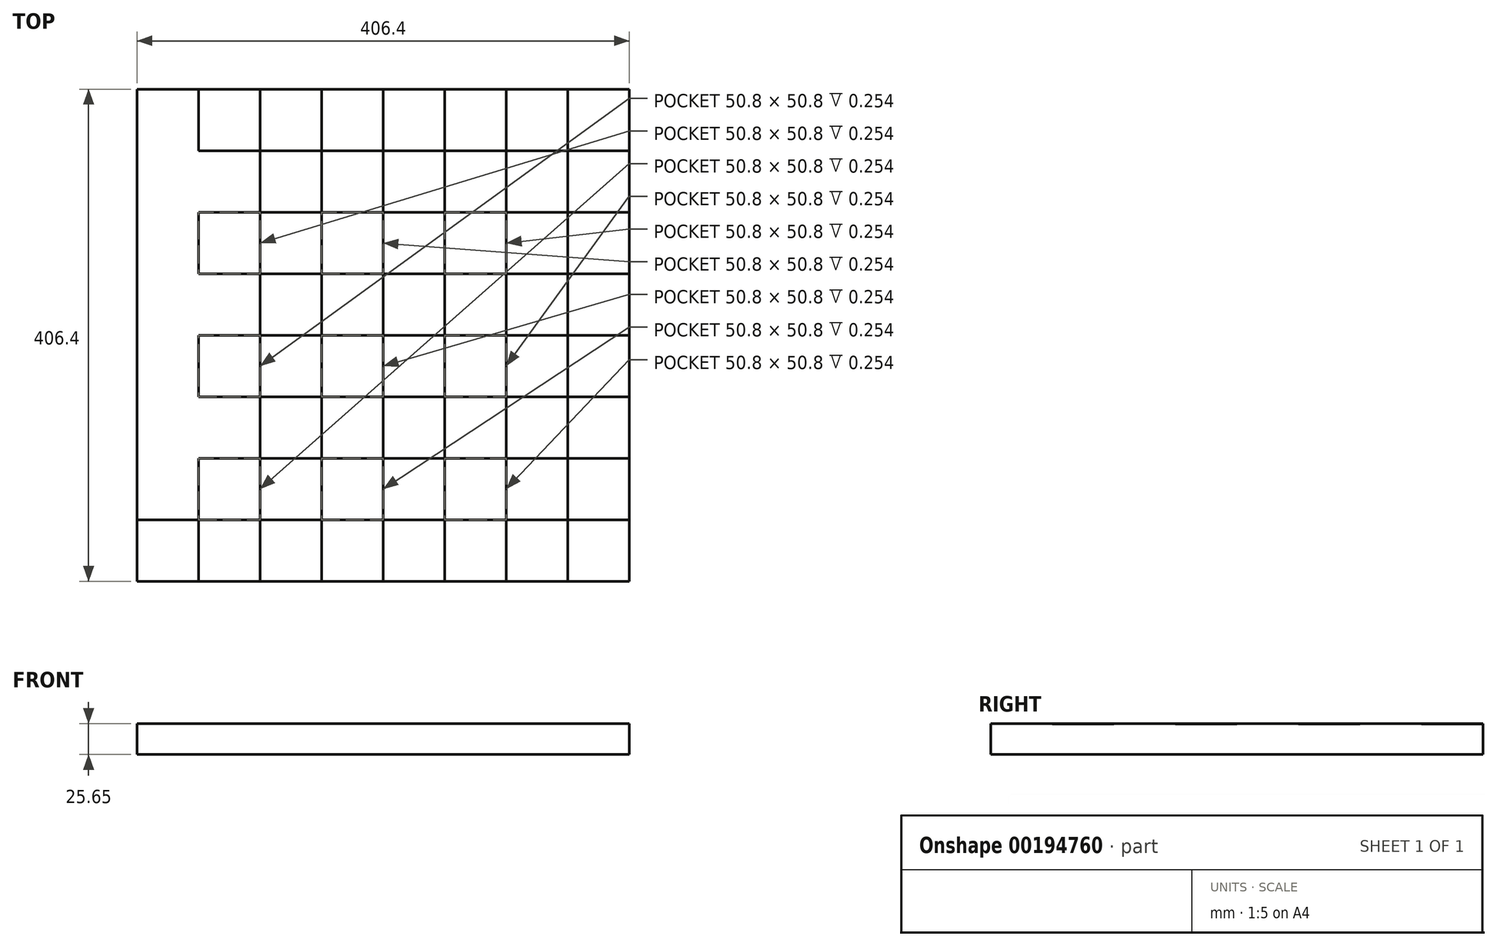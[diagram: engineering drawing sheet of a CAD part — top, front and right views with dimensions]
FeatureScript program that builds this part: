
annotation { "Feature Type Name" : "Feature", "Feature Type Description" : "" }
export const myFeature = defineFeature(function(context is Context, id is Id, definition is map)
    precondition{}
    {
        {
            var Q0;
            Q0=qCreatedBy(makeId("Top.planeOp"),FACE);
            var sketch = newSketch(context, id + "F0", { "sketchPlane" : qUnion([Q0])});
            skLineSegment(sketch, "E0.bottom", {"start": v(-124.17, 310.54) * mm, "end": v(282.23, 310.54) * mm});
            skLineSegment(sketch, "E0.top", {"start": v(-124.17, -95.86) * mm, "end": v(282.23, -95.86) * mm});
            skLineSegment(sketch, "E0.left", {"start": v(-124.17, 310.54) * mm, "end": v(-124.17, -95.86) * mm});
            skLineSegment(sketch, "E0.right", {"start": v(282.23, 310.54) * mm, "end": v(282.23, -95.86) * mm});
            skSolve(sketch);
        }
        {
            var Q0;
            Q0=makeQuery(id+"F0.imprint","IMPRINT",FACE,{"disambiguationData":[TD([[makeQuery(id+"F0.imprint","IMPRINT",EDGE,{"derivedFrom":sQuery(id+"F0.wireOp",EDGE,"E0.bottom")}),-1.0]])]});
            extrude(context, id + "F1", {"entities" : qUnion([Q0]), "depth" : 25.4 * mm});
        }
        {
            var Q0;
            Q0=makeQuery(id+"F1.opExtrude","CAP_FACE",FACE,{"disambiguationData":[OSD([sQuery(id+"F0.wireOp",EDGE,"E0.bottom"),sQuery(id+"F0.wireOp",EDGE,"E0.top"),sQuery(id+"F0.wireOp",EDGE,"E0.left"),sQuery(id+"F0.wireOp",EDGE,"E0.right")])],"isStart":false});
            var sketch = newSketch(context, id + "F2", { "sketchPlane" : qUnion([Q0])});
            skLineSegment(sketch, "E1.bottom", {"start": v(-124.17, 310.54) * mm, "end": v(-73.37, 310.54) * mm});
            skLineSegment(sketch, "E1.top", {"start": v(-124.17, 259.74) * mm, "end": v(-73.37, 259.74) * mm});
            skLineSegment(sketch, "E1.left", {"start": v(-124.17, 310.54) * mm, "end": v(-124.17, 259.74) * mm});
            skLineSegment(sketch, "E1.right", {"start": v(-73.37, 310.54) * mm, "end": v(-73.37, 259.74) * mm});
            skLineSegment(sketch, "E2.bottom", {"start": v(-73.37, 259.74) * mm, "end": v(-22.57, 259.74) * mm});
            skLineSegment(sketch, "E2.top", {"start": v(-73.37, 310.54) * mm, "end": v(-22.57, 310.54) * mm});
            skLineSegment(sketch, "E2.left", {"start": v(-73.37, 259.74) * mm, "end": v(-73.37, 310.54) * mm});
            skLineSegment(sketch, "E2.right", {"start": v(-22.57, 259.74) * mm, "end": v(-22.57, 310.54) * mm});
            skLineSegment(sketch, "E3.bottom", {"start": v(-22.57, 259.74) * mm, "end": v(28.23, 259.74) * mm});
            skLineSegment(sketch, "E3.top", {"start": v(-22.57, 310.54) * mm, "end": v(28.23, 310.54) * mm});
            skLineSegment(sketch, "E3.right", {"start": v(28.23, 259.74) * mm, "end": v(28.23, 310.54) * mm});
            skLineSegment(sketch, "E4.bottom", {"start": v(28.23, 259.74) * mm, "end": v(28.23, 259.74) * mm});
            skLineSegment(sketch, "E4.top", {"start": v(28.23, 310.54) * mm, "end": v(28.23, 310.54) * mm});
            skLineSegment(sketch, "E5.bottom", {"start": v(28.23, 259.74) * mm, "end": v(79.03, 259.74) * mm});
            skLineSegment(sketch, "E5.top", {"start": v(28.23, 310.54) * mm, "end": v(79.03, 310.54) * mm});
            skLineSegment(sketch, "E5.right", {"start": v(79.03, 259.74) * mm, "end": v(79.03, 310.54) * mm});
            skLineSegment(sketch, "E6.bottom", {"start": v(79.03, 259.74) * mm, "end": v(129.83, 259.74) * mm});
            skLineSegment(sketch, "E6.top", {"start": v(79.03, 310.54) * mm, "end": v(129.83, 310.54) * mm});
            skLineSegment(sketch, "E6.right", {"start": v(129.83, 259.74) * mm, "end": v(129.83, 310.54) * mm});
            skLineSegment(sketch, "E7.bottom", {"start": v(129.83, 259.74) * mm, "end": v(180.63, 259.74) * mm});
            skLineSegment(sketch, "E7.top", {"start": v(129.83, 310.54) * mm, "end": v(180.63, 310.54) * mm});
            skLineSegment(sketch, "E7.right", {"start": v(180.63, 259.74) * mm, "end": v(180.63, 310.54) * mm});
            skLineSegment(sketch, "E8.bottom", {"start": v(180.63, 259.74) * mm, "end": v(231.43, 259.74) * mm});
            skLineSegment(sketch, "E8.top", {"start": v(180.63, 310.54) * mm, "end": v(231.43, 310.54) * mm});
            skLineSegment(sketch, "E8.right", {"start": v(231.43, 259.74) * mm, "end": v(231.43, 310.54) * mm});
            skLineSegment(sketch, "E9.bottom", {"start": v(231.43, 259.74) * mm, "end": v(282.23, 259.74) * mm});
            skLineSegment(sketch, "E9.top", {"start": v(231.43, 310.54) * mm, "end": v(282.23, 310.54) * mm});
            skLineSegment(sketch, "E9.right", {"start": v(282.23, 259.74) * mm, "end": v(282.23, 310.54) * mm});
            skLineSegment(sketch, "E10.bottom", {"start": v(-124.17, -95.86) * mm, "end": v(-73.37, -95.86) * mm});
            skLineSegment(sketch, "E10.top", {"start": v(-124.17, -45.06) * mm, "end": v(-73.37, -45.06) * mm});
            skLineSegment(sketch, "E10.left", {"start": v(-124.17, -95.86) * mm, "end": v(-124.17, -45.06) * mm});
            skLineSegment(sketch, "E10.right", {"start": v(-73.37, -95.86) * mm, "end": v(-73.37, -45.06) * mm});
            skLineSegment(sketch, "E11.bottom", {"start": v(-73.37, -95.86) * mm, "end": v(-22.57, -95.86) * mm});
            skLineSegment(sketch, "E11.top", {"start": v(-73.37, -45.06) * mm, "end": v(-22.57, -45.06) * mm});
            skLineSegment(sketch, "E11.right", {"start": v(-22.57, -95.86) * mm, "end": v(-22.57, -45.06) * mm});
            skLineSegment(sketch, "E12.bottom", {"start": v(-22.57, -95.86) * mm, "end": v(28.23, -95.86) * mm});
            skLineSegment(sketch, "E12.top", {"start": v(-22.57, -45.06) * mm, "end": v(28.23, -45.06) * mm});
            skLineSegment(sketch, "E12.right", {"start": v(28.23, -95.86) * mm, "end": v(28.23, -45.06) * mm});
            skLineSegment(sketch, "E13.bottom", {"start": v(28.23, -95.86) * mm, "end": v(79.03, -95.86) * mm});
            skLineSegment(sketch, "E13.top", {"start": v(28.23, -45.06) * mm, "end": v(79.03, -45.06) * mm});
            skLineSegment(sketch, "E13.right", {"start": v(79.03, -95.86) * mm, "end": v(79.03, -45.06) * mm});
            skLineSegment(sketch, "E14.bottom", {"start": v(79.03, -95.86) * mm, "end": v(129.83, -95.86) * mm});
            skLineSegment(sketch, "E14.top", {"start": v(79.03, -45.06) * mm, "end": v(129.83, -45.06) * mm});
            skLineSegment(sketch, "E14.right", {"start": v(129.83, -95.86) * mm, "end": v(129.83, -45.06) * mm});
            skLineSegment(sketch, "E15.bottom", {"start": v(129.83, -95.86) * mm, "end": v(180.63, -95.86) * mm});
            skLineSegment(sketch, "E15.top", {"start": v(129.83, -45.06) * mm, "end": v(180.63, -45.06) * mm});
            skLineSegment(sketch, "E15.right", {"start": v(180.63, -95.86) * mm, "end": v(180.63, -45.06) * mm});
            skLineSegment(sketch, "E16.bottom", {"start": v(180.63, -95.86) * mm, "end": v(231.43, -95.86) * mm});
            skLineSegment(sketch, "E16.top", {"start": v(180.63, -45.06) * mm, "end": v(231.43, -45.06) * mm});
            skLineSegment(sketch, "E16.right", {"start": v(231.43, -95.86) * mm, "end": v(231.43, -45.06) * mm});
            skLineSegment(sketch, "E17.bottom", {"start": v(231.43, -95.86) * mm, "end": v(282.23, -95.86) * mm});
            skLineSegment(sketch, "E17.top", {"start": v(231.43, -45.06) * mm, "end": v(282.23, -45.06) * mm});
            skLineSegment(sketch, "E17.right", {"start": v(282.23, -95.86) * mm, "end": v(282.23, -45.06) * mm});
            skLineSegment(sketch, "E18.bottom", {"start": v(-73.37, 259.74) * mm, "end": v(-124.17, 259.74) * mm});
            skLineSegment(sketch, "E18.top", {"start": v(-73.37, 208.94) * mm, "end": v(-124.17, 208.94) * mm});
            skLineSegment(sketch, "E18.left", {"start": v(-73.37, 259.74) * mm, "end": v(-73.37, 208.94) * mm});
            skLineSegment(sketch, "E18.right", {"start": v(-124.17, 259.74) * mm, "end": v(-124.17, 208.94) * mm});
            skLineSegment(sketch, "E19.top", {"start": v(-73.37, 158.14) * mm, "end": v(-124.17, 158.14) * mm});
            skLineSegment(sketch, "E19.left", {"start": v(-73.37, 208.94) * mm, "end": v(-73.37, 158.14) * mm});
            skLineSegment(sketch, "E19.right", {"start": v(-124.17, 208.94) * mm, "end": v(-124.17, 158.14) * mm});
            skLineSegment(sketch, "E20.bottom", {"start": v(-124.17, 158.14) * mm, "end": v(-73.37, 158.14) * mm});
            skLineSegment(sketch, "E20.top", {"start": v(-124.17, 107.34) * mm, "end": v(-73.37, 107.34) * mm});
            skLineSegment(sketch, "E20.left", {"start": v(-124.17, 158.14) * mm, "end": v(-124.17, 107.34) * mm});
            skLineSegment(sketch, "E20.right", {"start": v(-73.37, 158.14) * mm, "end": v(-73.37, 107.34) * mm});
            skLineSegment(sketch, "E21.top", {"start": v(-124.17, 56.54) * mm, "end": v(-73.37, 56.54) * mm});
            skLineSegment(sketch, "E21.left", {"start": v(-124.17, 107.34) * mm, "end": v(-124.17, 56.54) * mm});
            skLineSegment(sketch, "E21.right", {"start": v(-73.37, 107.34) * mm, "end": v(-73.37, 56.54) * mm});
            skLineSegment(sketch, "E22.top", {"start": v(-124.17, 5.74) * mm, "end": v(-73.37, 5.74) * mm});
            skLineSegment(sketch, "E22.left", {"start": v(-124.17, 56.54) * mm, "end": v(-124.17, 5.74) * mm});
            skLineSegment(sketch, "E23.left", {"start": v(-124.17, 5.74) * mm, "end": v(-124.17, -45.06) * mm});
            skLineSegment(sketch, "E23.right", {"start": v(-73.37, 5.74) * mm, "end": v(-73.37, -45.06) * mm});
            skLineSegment(sketch, "E24.bottom", {"start": v(282.23, 259.74) * mm, "end": v(231.43, 259.74) * mm});
            skLineSegment(sketch, "E24.top", {"start": v(282.23, 208.94) * mm, "end": v(231.43, 208.94) * mm});
            skLineSegment(sketch, "E24.left", {"start": v(282.23, 259.74) * mm, "end": v(282.23, 208.94) * mm});
            skLineSegment(sketch, "E24.right", {"start": v(231.43, 259.74) * mm, "end": v(231.43, 208.94) * mm});
            skLineSegment(sketch, "E25.top", {"start": v(282.23, 158.14) * mm, "end": v(231.43, 158.14) * mm});
            skLineSegment(sketch, "E25.left", {"start": v(282.23, 208.94) * mm, "end": v(282.23, 158.14) * mm});
            skLineSegment(sketch, "E25.right", {"start": v(231.43, 208.94) * mm, "end": v(231.43, 158.14) * mm});
            skLineSegment(sketch, "E26.top", {"start": v(282.23, 107.34) * mm, "end": v(231.43, 107.34) * mm});
            skLineSegment(sketch, "E26.left", {"start": v(282.23, 158.14) * mm, "end": v(282.23, 107.34) * mm});
            skLineSegment(sketch, "E26.right", {"start": v(231.43, 158.14) * mm, "end": v(231.43, 107.34) * mm});
            skLineSegment(sketch, "E27.top", {"start": v(282.23, 56.54) * mm, "end": v(231.43, 56.54) * mm});
            skLineSegment(sketch, "E27.left", {"start": v(282.23, 107.34) * mm, "end": v(282.23, 56.54) * mm});
            skLineSegment(sketch, "E27.right", {"start": v(231.43, 107.34) * mm, "end": v(231.43, 56.54) * mm});
            skLineSegment(sketch, "E28.right", {"start": v(-73.37, 56.54) * mm, "end": v(-73.37, 5.74) * mm});
            skLineSegment(sketch, "E29.top", {"start": v(282.23, 5.74) * mm, "end": v(231.43, 5.74) * mm});
            skLineSegment(sketch, "E29.left", {"start": v(282.23, 56.54) * mm, "end": v(282.23, 5.74) * mm});
            skLineSegment(sketch, "E29.right", {"start": v(231.43, 56.54) * mm, "end": v(231.43, 5.74) * mm});
            skLineSegment(sketch, "E30.top", {"start": v(282.23, -45.06) * mm, "end": v(231.43, -45.06) * mm});
            skLineSegment(sketch, "E30.left", {"start": v(282.23, 5.74) * mm, "end": v(282.23, -45.06) * mm});
            skLineSegment(sketch, "E30.right", {"start": v(231.43, 5.74) * mm, "end": v(231.43, -45.06) * mm});
            skLineSegment(sketch, "E31", {"start": v(-22.57, 259.74) * mm, "end": v(-22.57, -45.06) * mm});
            skLineSegment(sketch, "E32", {"start": v(28.23, 259.74) * mm, "end": v(28.23, -45.06) * mm});
            skLineSegment(sketch, "E33", {"start": v(79.03, 259.74) * mm, "end": v(79.03, -45.06) * mm});
            skLineSegment(sketch, "E34", {"start": v(129.83, 259.74) * mm, "end": v(129.83, -45.06) * mm});
            skLineSegment(sketch, "E35", {"start": v(180.63, 259.74) * mm, "end": v(180.63, -45.06) * mm});
            skLineSegment(sketch, "E36", {"start": v(-73.37, 208.94) * mm, "end": v(231.43, 208.94) * mm});
            skLineSegment(sketch, "E37", {"start": v(-73.37, 158.14) * mm, "end": v(231.43, 158.14) * mm});
            skLineSegment(sketch, "E38", {"start": v(-73.37, 107.34) * mm, "end": v(231.43, 107.34) * mm});
            skLineSegment(sketch, "E39", {"start": v(-73.37, 56.54) * mm, "end": v(231.43, 56.54) * mm});
            skLineSegment(sketch, "E40", {"start": v(-73.37, 5.74) * mm, "end": v(231.43, 5.74) * mm});
            skSolve(sketch);
        }
        {
            var Q0;
            Q0=makeQuery(id+"F2.imprint","IMPRINT",FACE,{"disambiguationData":[TD([[makeQuery(id+"F2.imprint","IMPRINT",EDGE,{"derivedFrom":sQuery(id+"F2.wireOp",EDGE,"E10.bottom")}),1.0]])]});
            var Q1;
            Q1=makeQuery(id+"F2.imprint","IMPRINT",FACE,{"disambiguationData":[TD([[makeQuery(id+"F2.imprint","IMPRINT",EDGE,{"derivedFrom":sQuery(id+"F2.wireOp",EDGE,"E21.top")}),-1.0]])]});
            var Q2;
            Q2=makeQuery(id+"F2.imprint","IMPRINT",FACE,{"disambiguationData":[TD([[makeQuery(id+"F2.imprint","IMPRINT",EDGE,{"derivedFrom":sQuery(id+"F2.wireOp",EDGE,"E20.bottom")}),-1.0]])]});
            var Q3;
            Q3=makeQuery(id+"F2.imprint","IMPRINT",FACE,{"disambiguationData":[TD([[makeQuery(id+"F2.imprint","IMPRINT",EDGE,{"derivedFrom":sQuery(id+"F2.wireOp",EDGE,"E18.bottom")}),1.0]])]});
            var Q4;
            Q4=makeQuery(id+"F2.imprint","IMPRINT",FACE,{"disambiguationData":[TD([[makeQuery(id+"F2.imprint","IMPRINT",EDGE,{"derivedFrom":sQuery(id+"F2.wireOp",EDGE,"E12.bottom")}),1.0]])]});
            var Q5;
            {var subQ0=sQuery(id+"F2.wireOp",EDGE,"E39");var subQ1=sQuery(id+"F2.wireOp",EDGE,"E31");var subQ2=makeQuery(id+"F2.imprint","INTERSECT",VERTEX,{"derivedFrom":[subQ1,subQ0]});Q5=makeQuery(id+"F2.imprint","IMPRINT",FACE,{"disambiguationData":[TD([[makeQuery(id+"F2.imprint","IMPRINT",EDGE,{"disambiguationData":[TD([[subQ2,-1.0]])],"derivedFrom":subQ1}),1.0]])]});}
            var Q6;
            {var subQ0=sQuery(id+"F2.wireOp",EDGE,"E37");var subQ1=sQuery(id+"F2.wireOp",EDGE,"E31");var subQ2=makeQuery(id+"F2.imprint","INTERSECT",VERTEX,{"derivedFrom":[subQ1,subQ0]});Q6=makeQuery(id+"F2.imprint","IMPRINT",FACE,{"disambiguationData":[TD([[makeQuery(id+"F2.imprint","IMPRINT",EDGE,{"disambiguationData":[TD([[subQ2,-1.0]])],"derivedFrom":subQ1}),1.0]])]});}
            var Q7;
            {var subQ0=sQuery(id+"F2.wireOp",EDGE,"E3.bottom");Q7=makeQuery(id+"F2.imprint","IMPRINT",FACE,{"disambiguationData":[TD([[makeQuery(id+"F2.imprint","IMPRINT",EDGE,{"derivedFrom":subQ0}),-1.0]])]});}
            var Q8;
            Q8=makeQuery(id+"F2.imprint","IMPRINT",FACE,{"disambiguationData":[TD([[makeQuery(id+"F2.imprint","IMPRINT",EDGE,{"derivedFrom":sQuery(id+"F2.wireOp",EDGE,"E14.bottom")}),1.0]])]});
            var Q9;
            {var subQ0=sQuery(id+"F2.wireOp",EDGE,"E39");var subQ1=sQuery(id+"F2.wireOp",EDGE,"E33");var subQ2=makeQuery(id+"F2.imprint","INTERSECT",VERTEX,{"derivedFrom":[subQ1,subQ0]});Q9=makeQuery(id+"F2.imprint","IMPRINT",FACE,{"disambiguationData":[TD([[makeQuery(id+"F2.imprint","IMPRINT",EDGE,{"disambiguationData":[TD([[subQ2,-1.0]])],"derivedFrom":subQ1}),1.0]])]});}
            var Q10;
            {var subQ0=sQuery(id+"F2.wireOp",EDGE,"E37");var subQ1=sQuery(id+"F2.wireOp",EDGE,"E33");var subQ2=makeQuery(id+"F2.imprint","INTERSECT",VERTEX,{"derivedFrom":[subQ1,subQ0]});Q10=makeQuery(id+"F2.imprint","IMPRINT",FACE,{"disambiguationData":[TD([[makeQuery(id+"F2.imprint","IMPRINT",EDGE,{"disambiguationData":[TD([[subQ2,-1.0]])],"derivedFrom":subQ1}),1.0]])]});}
            var Q11;
            {var subQ0=sQuery(id+"F2.wireOp",EDGE,"E6.bottom");Q11=makeQuery(id+"F2.imprint","IMPRINT",FACE,{"disambiguationData":[TD([[makeQuery(id+"F2.imprint","IMPRINT",EDGE,{"derivedFrom":subQ0}),-1.0]])]});}
            var Q12;
            Q12=makeQuery(id+"F2.imprint","IMPRINT",FACE,{"disambiguationData":[TD([[makeQuery(id+"F2.imprint","IMPRINT",EDGE,{"derivedFrom":sQuery(id+"F2.wireOp",EDGE,"E16.bottom")}),1.0]])]});
            var Q13;
            {var subQ0=sQuery(id+"F2.wireOp",EDGE,"E29.right");Q13=makeQuery(id+"F2.imprint","IMPRINT",FACE,{"disambiguationData":[TD([[makeQuery(id+"F2.imprint","IMPRINT",EDGE,{"derivedFrom":subQ0}),-1.0]])]});}
            var Q14;
            {var subQ0=sQuery(id+"F2.wireOp",EDGE,"E26.right");Q14=makeQuery(id+"F2.imprint","IMPRINT",FACE,{"disambiguationData":[TD([[makeQuery(id+"F2.imprint","IMPRINT",EDGE,{"derivedFrom":subQ0}),-1.0]])]});}
            var Q15;
            {var subQ0=sQuery(id+"F2.wireOp",EDGE,"E8.bottom");Q15=makeQuery(id+"F2.imprint","IMPRINT",FACE,{"disambiguationData":[TD([[makeQuery(id+"F2.imprint","IMPRINT",EDGE,{"derivedFrom":subQ0}),-1.0]])]});}
            var Q16;
            Q16=sQuery(id+"F2.wireOp",EDGE,"E10.left");
            extrude(context, id + "F3", {"entities" : qUnion([Q0, Q1, Q2, Q3, Q4, Q5, Q6, Q7, Q8, Q9, Q10, Q11, Q12, Q13, Q14, Q15]), "operationType" : NewBodyOperationType.ADD, "surfaceEntities" : qUnion([Q16]), "depth" : 0.25 * mm, "hasSecondDirection" : true, "secondDirectionOppositeDirection" : true, "secondDirectionDepth" : 25.4 * mm});
        }
        {
            var Q0;
            Q0=makeQuery(id+"F1.opExtrude","CAP_FACE",FACE,{"disambiguationData":[OSD([sQuery(id+"F0.wireOp",EDGE,"E0.bottom"),sQuery(id+"F0.wireOp",EDGE,"E0.top"),sQuery(id+"F0.wireOp",EDGE,"E0.left"),sQuery(id+"F0.wireOp",EDGE,"E0.right")])],"isStart":false});
            var sketch = newSketch(context, id + "F4", { "sketchPlane" : qUnion([Q0])});
            skLineSegment(sketch, "E41.bottom", {"start": v(-73.37, 259.74) * mm, "end": v(-22.57, 259.74) * mm});
            skLineSegment(sketch, "E41.top", {"start": v(-73.37, 310.54) * mm, "end": v(-22.57, 310.54) * mm});
            skLineSegment(sketch, "E41.left", {"start": v(-73.37, 259.74) * mm, "end": v(-73.37, 310.54) * mm});
            skLineSegment(sketch, "E41.right", {"start": v(-22.57, 259.74) * mm, "end": v(-22.57, 310.54) * mm});
            skLineSegment(sketch, "E42.bottom", {"start": v(-73.37, 208.94) * mm, "end": v(-22.57, 208.94) * mm});
            skLineSegment(sketch, "E42.top", {"start": v(-73.37, 158.14) * mm, "end": v(-22.57, 158.14) * mm});
            skLineSegment(sketch, "E42.left", {"start": v(-73.37, 208.94) * mm, "end": v(-73.37, 158.14) * mm});
            skLineSegment(sketch, "E42.right", {"start": v(-22.57, 208.94) * mm, "end": v(-22.57, 158.14) * mm});
            skLineSegment(sketch, "E43.bottom", {"start": v(-73.37, 107.34) * mm, "end": v(-22.57, 107.34) * mm});
            skLineSegment(sketch, "E43.top", {"start": v(-73.37, 56.54) * mm, "end": v(-22.57, 56.54) * mm});
            skLineSegment(sketch, "E43.left", {"start": v(-73.37, 107.34) * mm, "end": v(-73.37, 56.54) * mm});
            skLineSegment(sketch, "E43.right", {"start": v(-22.57, 107.34) * mm, "end": v(-22.57, 56.54) * mm});
            skLineSegment(sketch, "E44.bottom", {"start": v(-73.37, 5.74) * mm, "end": v(-22.57, 5.74) * mm});
            skLineSegment(sketch, "E44.top", {"start": v(-73.37, -45.06) * mm, "end": v(-22.57, -45.06) * mm});
            skLineSegment(sketch, "E44.left", {"start": v(-73.37, 5.74) * mm, "end": v(-73.37, -45.06) * mm});
            skLineSegment(sketch, "E44.right", {"start": v(-22.57, 5.74) * mm, "end": v(-22.57, -45.06) * mm});
            skLineSegment(sketch, "E45.bottom", {"start": v(28.23, 259.74) * mm, "end": v(79.03, 259.74) * mm});
            skLineSegment(sketch, "E45.top", {"start": v(28.23, 310.54) * mm, "end": v(79.03, 310.54) * mm});
            skLineSegment(sketch, "E45.left", {"start": v(28.23, 259.74) * mm, "end": v(28.23, 310.54) * mm});
            skLineSegment(sketch, "E45.right", {"start": v(79.03, 259.74) * mm, "end": v(79.03, 310.54) * mm});
            skLineSegment(sketch, "E46.bottom", {"start": v(28.23, 208.94) * mm, "end": v(79.03, 208.94) * mm});
            skLineSegment(sketch, "E46.top", {"start": v(28.23, 158.14) * mm, "end": v(79.03, 158.14) * mm});
            skLineSegment(sketch, "E46.left", {"start": v(28.23, 208.94) * mm, "end": v(28.23, 158.14) * mm});
            skLineSegment(sketch, "E46.right", {"start": v(79.03, 208.94) * mm, "end": v(79.03, 158.14) * mm});
            skLineSegment(sketch, "E47.bottom", {"start": v(28.23, 107.34) * mm, "end": v(79.03, 107.34) * mm});
            skLineSegment(sketch, "E47.top", {"start": v(28.23, 56.54) * mm, "end": v(79.03, 56.54) * mm});
            skLineSegment(sketch, "E47.left", {"start": v(28.23, 107.34) * mm, "end": v(28.23, 56.54) * mm});
            skLineSegment(sketch, "E47.right", {"start": v(79.03, 107.34) * mm, "end": v(79.03, 56.54) * mm});
            skLineSegment(sketch, "E48.bottom", {"start": v(28.23, 5.74) * mm, "end": v(79.03, 5.74) * mm});
            skLineSegment(sketch, "E48.top", {"start": v(28.23, -45.06) * mm, "end": v(79.03, -45.06) * mm});
            skLineSegment(sketch, "E48.left", {"start": v(28.23, 5.74) * mm, "end": v(28.23, -45.06) * mm});
            skLineSegment(sketch, "E48.right", {"start": v(79.03, 5.74) * mm, "end": v(79.03, -45.06) * mm});
            skLineSegment(sketch, "E49.bottom", {"start": v(129.83, -45.06) * mm, "end": v(180.63, -45.06) * mm});
            skLineSegment(sketch, "E49.top", {"start": v(129.83, 5.74) * mm, "end": v(180.63, 5.74) * mm});
            skLineSegment(sketch, "E49.left", {"start": v(129.83, -45.06) * mm, "end": v(129.83, 5.74) * mm});
            skLineSegment(sketch, "E49.right", {"start": v(180.63, -45.06) * mm, "end": v(180.63, 5.74) * mm});
            skLineSegment(sketch, "E50.bottom", {"start": v(180.63, 56.54) * mm, "end": v(129.83, 56.54) * mm});
            skLineSegment(sketch, "E50.top", {"start": v(180.63, 107.34) * mm, "end": v(129.83, 107.34) * mm});
            skLineSegment(sketch, "E50.left", {"start": v(180.63, 56.54) * mm, "end": v(180.63, 107.34) * mm});
            skLineSegment(sketch, "E50.right", {"start": v(129.83, 56.54) * mm, "end": v(129.83, 107.34) * mm});
            skLineSegment(sketch, "E51.bottom", {"start": v(129.83, 158.14) * mm, "end": v(180.63, 158.14) * mm});
            skLineSegment(sketch, "E51.top", {"start": v(129.83, 208.94) * mm, "end": v(180.63, 208.94) * mm});
            skLineSegment(sketch, "E51.left", {"start": v(129.83, 158.14) * mm, "end": v(129.83, 208.94) * mm});
            skLineSegment(sketch, "E51.right", {"start": v(180.63, 158.14) * mm, "end": v(180.63, 208.94) * mm});
            skLineSegment(sketch, "E52.bottom", {"start": v(129.83, 259.74) * mm, "end": v(180.63, 259.74) * mm});
            skLineSegment(sketch, "E52.top", {"start": v(129.83, 310.54) * mm, "end": v(180.63, 310.54) * mm});
            skLineSegment(sketch, "E52.left", {"start": v(129.83, 259.74) * mm, "end": v(129.83, 310.54) * mm});
            skLineSegment(sketch, "E52.right", {"start": v(180.63, 259.74) * mm, "end": v(180.63, 310.54) * mm});
            skLineSegment(sketch, "E53.bottom", {"start": v(231.43, 259.74) * mm, "end": v(282.23, 259.74) * mm});
            skLineSegment(sketch, "E53.top", {"start": v(231.43, 310.54) * mm, "end": v(282.23, 310.54) * mm});
            skLineSegment(sketch, "E53.left", {"start": v(231.43, 259.74) * mm, "end": v(231.43, 310.54) * mm});
            skLineSegment(sketch, "E53.right", {"start": v(282.23, 259.74) * mm, "end": v(282.23, 310.54) * mm});
            skLineSegment(sketch, "E54.bottom", {"start": v(231.43, 208.94) * mm, "end": v(282.23, 208.94) * mm});
            skLineSegment(sketch, "E54.top", {"start": v(231.43, 158.14) * mm, "end": v(282.23, 158.14) * mm});
            skLineSegment(sketch, "E54.left", {"start": v(231.43, 208.94) * mm, "end": v(231.43, 158.14) * mm});
            skLineSegment(sketch, "E54.right", {"start": v(282.23, 208.94) * mm, "end": v(282.23, 158.14) * mm});
            skLineSegment(sketch, "E55.bottom", {"start": v(231.43, 107.34) * mm, "end": v(282.23, 107.34) * mm});
            skLineSegment(sketch, "E55.top", {"start": v(231.43, 56.54) * mm, "end": v(282.23, 56.54) * mm});
            skLineSegment(sketch, "E55.left", {"start": v(231.43, 107.34) * mm, "end": v(231.43, 56.54) * mm});
            skLineSegment(sketch, "E55.right", {"start": v(282.23, 107.34) * mm, "end": v(282.23, 56.54) * mm});
            skLineSegment(sketch, "E56.bottom", {"start": v(231.43, 5.74) * mm, "end": v(282.23, 5.74) * mm});
            skLineSegment(sketch, "E56.top", {"start": v(231.43, -45.06) * mm, "end": v(282.23, -45.06) * mm});
            skLineSegment(sketch, "E56.left", {"start": v(231.43, 5.74) * mm, "end": v(231.43, -45.06) * mm});
            skLineSegment(sketch, "E56.right", {"start": v(282.23, 5.74) * mm, "end": v(282.23, -45.06) * mm});
            skSolve(sketch);
        }
        {
            var Q0;
            Q0=makeQuery(id+"F4.imprint","IMPRINT",FACE,{"disambiguationData":[TD([[makeQuery(id+"F4.imprint","IMPRINT",EDGE,{"derivedFrom":sQuery(id+"F4.wireOp",EDGE,"E44.bottom")}),-1.0]])]});
            var Q1;
            Q1=makeQuery(id+"F4.imprint","IMPRINT",FACE,{"disambiguationData":[TD([[makeQuery(id+"F4.imprint","IMPRINT",EDGE,{"derivedFrom":sQuery(id+"F4.wireOp",EDGE,"E43.bottom")}),-1.0]])]});
            var Q2;
            Q2=makeQuery(id+"F4.imprint","IMPRINT",FACE,{"disambiguationData":[TD([[makeQuery(id+"F4.imprint","IMPRINT",EDGE,{"derivedFrom":sQuery(id+"F4.wireOp",EDGE,"E42.bottom")}),-1.0]])]});
            var Q3;
            Q3=makeQuery(id+"F4.imprint","IMPRINT",FACE,{"disambiguationData":[TD([[makeQuery(id+"F4.imprint","IMPRINT",EDGE,{"derivedFrom":sQuery(id+"F4.wireOp",EDGE,"E41.bottom")}),1.0]])]});
            var Q4;
            Q4=makeQuery(id+"F4.imprint","IMPRINT",FACE,{"disambiguationData":[TD([[makeQuery(id+"F4.imprint","IMPRINT",EDGE,{"derivedFrom":sQuery(id+"F4.wireOp",EDGE,"E45.bottom")}),1.0]])]});
            var Q5;
            Q5=makeQuery(id+"F4.imprint","IMPRINT",FACE,{"disambiguationData":[TD([[makeQuery(id+"F4.imprint","IMPRINT",EDGE,{"derivedFrom":sQuery(id+"F4.wireOp",EDGE,"E46.bottom")}),-1.0]])]});
            var Q6;
            Q6=makeQuery(id+"F4.imprint","IMPRINT",FACE,{"disambiguationData":[TD([[makeQuery(id+"F4.imprint","IMPRINT",EDGE,{"derivedFrom":sQuery(id+"F4.wireOp",EDGE,"E47.bottom")}),-1.0]])]});
            var Q7;
            Q7=makeQuery(id+"F4.imprint","IMPRINT",FACE,{"disambiguationData":[TD([[makeQuery(id+"F4.imprint","IMPRINT",EDGE,{"derivedFrom":sQuery(id+"F4.wireOp",EDGE,"E48.bottom")}),-1.0]])]});
            var Q8;
            Q8=makeQuery(id+"F4.imprint","IMPRINT",FACE,{"disambiguationData":[TD([[makeQuery(id+"F4.imprint","IMPRINT",EDGE,{"derivedFrom":sQuery(id+"F4.wireOp",EDGE,"E49.bottom")}),1.0]])]});
            var Q9;
            Q9=makeQuery(id+"F4.imprint","IMPRINT",FACE,{"disambiguationData":[TD([[makeQuery(id+"F4.imprint","IMPRINT",EDGE,{"derivedFrom":sQuery(id+"F4.wireOp",EDGE,"E50.bottom")}),-1.0]])]});
            var Q10;
            Q10=makeQuery(id+"F4.imprint","IMPRINT",FACE,{"disambiguationData":[TD([[makeQuery(id+"F4.imprint","IMPRINT",EDGE,{"derivedFrom":sQuery(id+"F4.wireOp",EDGE,"E51.bottom")}),1.0]])]});
            var Q11;
            Q11=makeQuery(id+"F4.imprint","IMPRINT",FACE,{"disambiguationData":[TD([[makeQuery(id+"F4.imprint","IMPRINT",EDGE,{"derivedFrom":sQuery(id+"F4.wireOp",EDGE,"E52.bottom")}),1.0]])]});
            var Q12;
            Q12=makeQuery(id+"F4.imprint","IMPRINT",FACE,{"disambiguationData":[TD([[makeQuery(id+"F4.imprint","IMPRINT",EDGE,{"derivedFrom":sQuery(id+"F4.wireOp",EDGE,"E53.bottom")}),1.0]])]});
            var Q13;
            Q13=makeQuery(id+"F4.imprint","IMPRINT",FACE,{"disambiguationData":[TD([[makeQuery(id+"F4.imprint","IMPRINT",EDGE,{"derivedFrom":sQuery(id+"F4.wireOp",EDGE,"E54.bottom")}),-1.0]])]});
            var Q14;
            Q14=makeQuery(id+"F4.imprint","IMPRINT",FACE,{"disambiguationData":[TD([[makeQuery(id+"F4.imprint","IMPRINT",EDGE,{"derivedFrom":sQuery(id+"F4.wireOp",EDGE,"E55.bottom")}),-1.0]])]});
            var Q15;
            Q15=makeQuery(id+"F4.imprint","IMPRINT",FACE,{"disambiguationData":[TD([[makeQuery(id+"F4.imprint","IMPRINT",EDGE,{"derivedFrom":sQuery(id+"F4.wireOp",EDGE,"E56.bottom")}),-1.0]])]});
            extrude(context, id + "F5", {"entities" : qUnion([Q0, Q1, Q2, Q3, Q4, Q5, Q6, Q7, Q8, Q9, Q10, Q11, Q12, Q13, Q14, Q15]), "operationType" : NewBodyOperationType.REMOVE, "oppositeDirection" : true, "depth" : 0.25 * mm});
        }
    });
